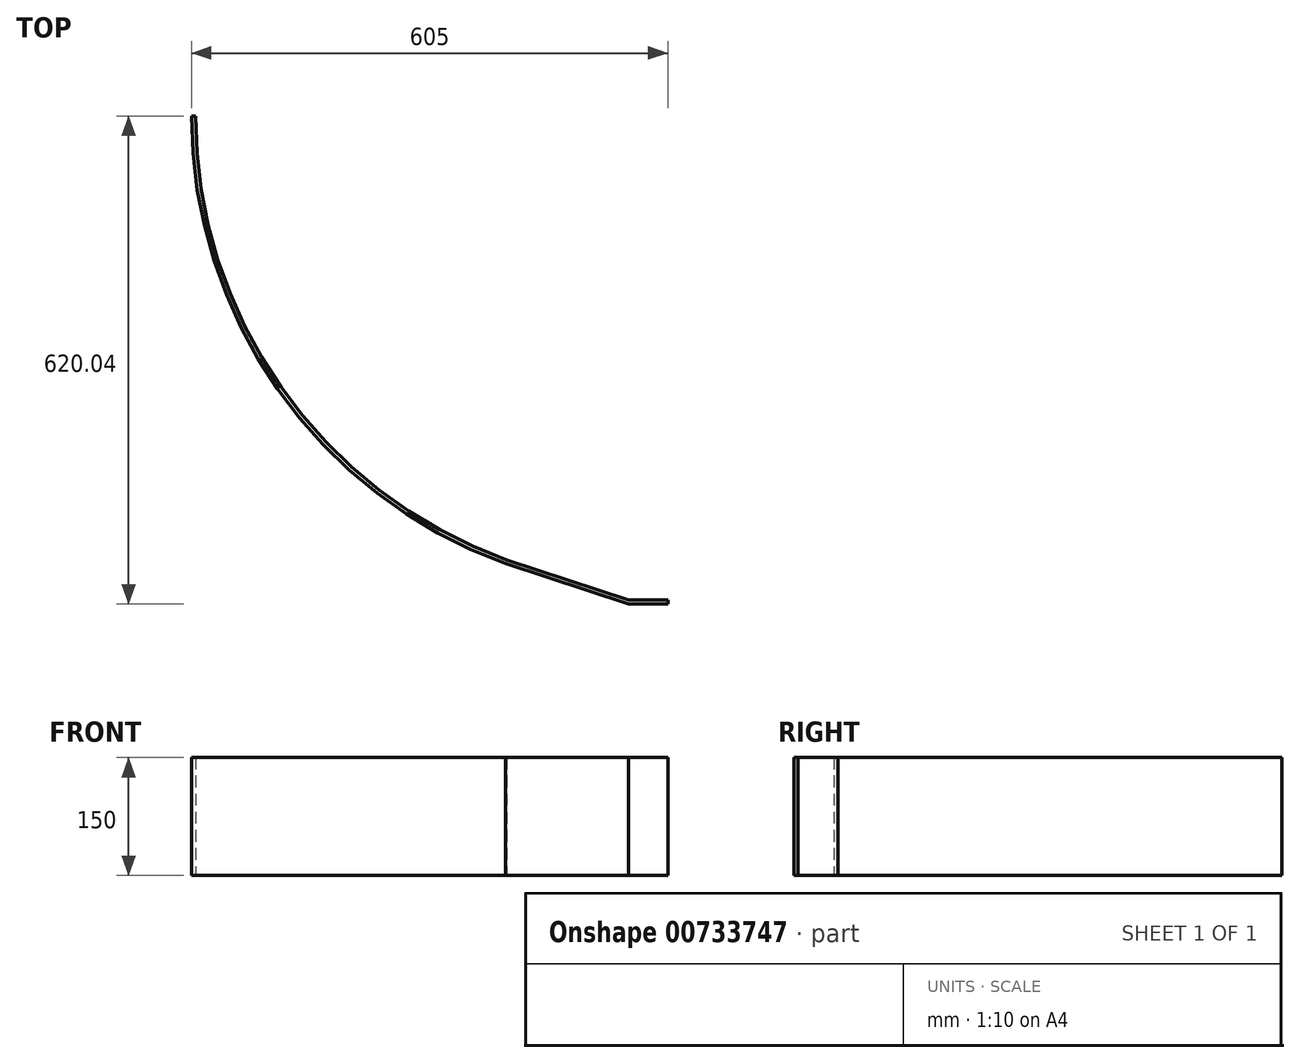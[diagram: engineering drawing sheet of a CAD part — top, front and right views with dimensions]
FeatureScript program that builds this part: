
annotation { "Feature Type Name" : "Feature", "Feature Type Description" : "" }
export const myFeature = defineFeature(function(context is Context, id is Id, definition is map)
    precondition{}
    {
        {
            var Q0;
            Q0=qCreatedBy(makeId("Top.planeOp"),FACE);
            var sketch = newSketch(context, id + "F0", { "sketchPlane" : qUnion([Q0])});
            skArc(sketch, "E0", {"start": v(-600, 0) * mm, "mid": v(-491.33, -344.38) * mm, "end": v(-204.67, -564.01) * mm});
            skArc(sketch, "E1", {"start": v(-605, 0) * mm, "mid": v(-495.42, -347.25) * mm, "end": v(-206.38, -568.71) * mm});
            skLineSegment(sketch, "E2", {"start": v(0, 600) * mm, "end": v(0, 605) * mm});
            skLineSegment(sketch, "E3", {"start": v(0, 0) * mm, "end": v(0, -605) * mm});
            skLineSegment(sketch, "E4", {"start": v(0, 0) * mm, "end": v(-605, 0) * mm});
            skLineSegment(sketch, "E5", {"start": v(0, -605) * mm, "end": v(0, -615) * mm});
            skLineSegment(sketch, "E6", {"start": v(0, -615) * mm, "end": v(5, -615) * mm});
            skLineSegment(sketch, "E7.top", {"start": v(0, -620.04) * mm, "end": v(5, -620.04) * mm});
            skLineSegment(sketch, "E7.left", {"start": v(0, -615) * mm, "end": v(0, -620.04) * mm});
            skLineSegment(sketch, "E7.right", {"start": v(5, -615) * mm, "end": v(5, -620.04) * mm});
            skLineSegment(sketch, "E8", {"start": v(-104.85, -595.84) * mm, "end": v(-104.13, -590.9) * mm});
            skLineSegment(sketch, "E9", {"start": v(0, -615) * mm, "end": v(-50, -615) * mm});
            skLineSegment(sketch, "E10", {"start": v(-50, -615) * mm, "end": v(-50, -620) * mm});
            skLineSegment(sketch, "E11", {"start": v(-50, -620) * mm, "end": v(0, -620.04) * mm});
            skLineSegment(sketch, "E12", {"start": v(-206.38, -568.71) * mm, "end": v(-204.67, -564.01) * mm});
            skLineSegment(sketch, "E13", {"start": v(-204.67, -564.01) * mm, "end": v(-50, -615) * mm});
            skLineSegment(sketch, "E14", {"start": v(-206.38, -568.71) * mm, "end": v(-50, -620) * mm});
            skSolve(sketch);
        }
        {
            var Q0;
            {var subQ0=sQuery(id+"F0.wireOp",EDGE,"E0");Q0=makeQuery(id+"F0.imprint","IMPRINT",FACE,{"disambiguationData":[TD([[makeQuery(id+"F0.imprint","IMPRINT",EDGE,{"derivedFrom":subQ0}),-1.0]])]});}
            var Q1;
            Q1=makeQuery(id+"F0.imprint","IMPRINT",FACE,{"disambiguationData":[TD([[makeQuery(id+"F0.imprint","IMPRINT",EDGE,{"derivedFrom":sQuery(id+"F0.wireOp",EDGE,"E10")}),-1.0]])]});
            var Q2;
            Q2=makeQuery(id+"F0.imprint","IMPRINT",FACE,{"disambiguationData":[TD([[makeQuery(id+"F0.imprint","IMPRINT",EDGE,{"derivedFrom":sQuery(id+"F0.wireOp",EDGE,"E7.left")}),-1.0]])]});
            extrude(context, id + "F1", {"entities" : qUnion([Q0, Q1, Q2]), "depth" : 150 * mm, "offsetDistance" : 25 * mm});
        }
    });
